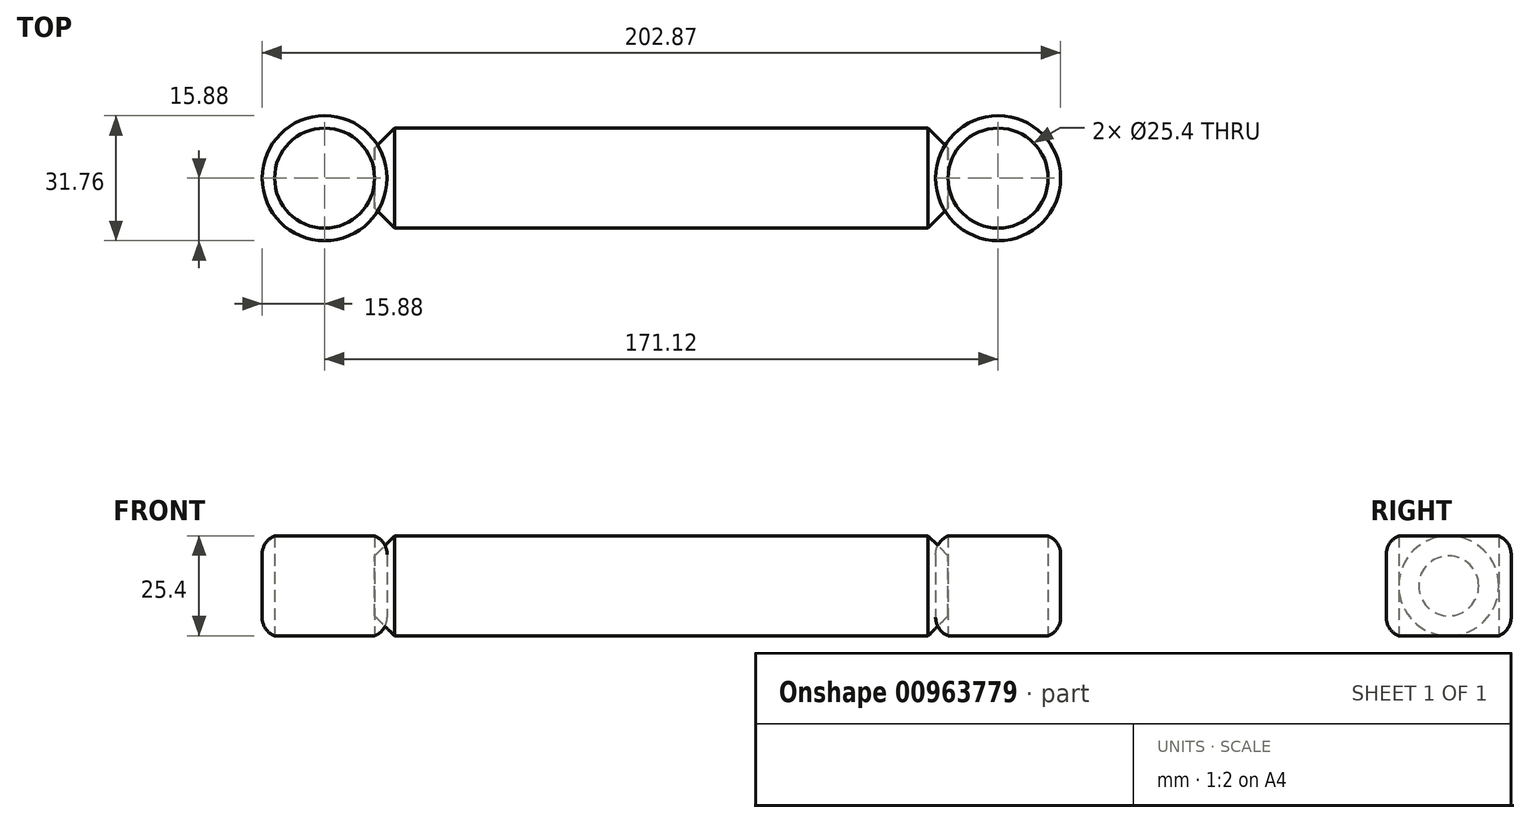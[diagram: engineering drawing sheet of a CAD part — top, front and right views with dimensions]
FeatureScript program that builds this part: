
annotation { "Feature Type Name" : "Feature", "Feature Type Description" : "" }
export const myFeature = defineFeature(function(context is Context, id is Id, definition is map)
    precondition{}
    {
        {
            var Q0;
            Q0=qCreatedBy(makeId("Top.planeOp"),FACE);
            var sketch = newSketch(context, id + "F0", { "sketchPlane" : qUnion([Q0])});
            skCircle(sketch, "E0", {"center": v(0, 0) * mm, "radius": 12.7 * mm});
            skCircle(sketch, "E1", {"center": v(171.12, 0) * mm, "radius": 12.7 * mm});
            skLineSegment(sketch, "E2", {"start": v(15.88, 0) * mm, "end": v(155.24, 0) * mm});
            skCircle(sketch, "E3", {"center": v(0, 0) * mm, "radius": 15.88 * mm});
            skCircle(sketch, "E4", {"center": v(171.12, 0) * mm, "radius": 15.88 * mm});
            skLineSegment(sketch, "E5", {"start": v(155.24, 0) * mm, "end": v(158.42, 0) * mm});
            skLineSegment(sketch, "E6", {"start": v(15.88, 0) * mm, "end": v(12.7, 0) * mm});
            skSolve(sketch);
        }
        {
            var Q0;
            Q0 = qSketchRegion(id + "F0", true);
            extrude(context, id + "F1", {"entities" : qUnion([Q0]), "endBound" : BoundingType.SYMMETRIC, "depth" : 25.4 * mm, "offsetDistance" : 25.4 * mm});
        }
        {
            var Q0;
            Q0=qCreatedBy(makeId("Right.planeOp"),FACE);
            cPlane(context, id + "F2", {"entities" : qUnion([Q0]), "cplaneType" : CPlaneType.OFFSET, "offset" : 12.7 * mm, "width" : 152.4 * mm, "height" : 152.4 * mm});
        }
        {
            var Q0;
            Q0=qCreatedBy(id+"F2.planeOp",FACE);
            var sketch = newSketch(context, id + "F3", { "sketchPlane" : qUnion([Q0])});
            skCircle(sketch, "E7", {"center": v(0, 0) * mm, "radius": 12.7 * mm});
            skSolve(sketch);
        }
        {
            var Q0;
            Q0 = qSketchRegion(id + "F3", true);
            var Q1;
            Q1=sQuery(id+"F0.wireOp",EDGE,"E6");
            var Q2;
            Q2=sQuery(id+"F0.wireOp",EDGE,"E2");
            var Q3;
            Q3=sQuery(id+"F0.wireOp",EDGE,"E5");
            sweep(context, id + "F4", {"profiles" : qUnion([Q0]), "path" : qUnion([Q1, Q2, Q3])});
        }
        {
            var Q0;
            Q0=makeQuery(id+"F1.opExtrude","CAP_EDGE",EDGE,{"disambiguationData":[OSD([sQuery(id+"F0.wireOp",EDGE,"E3")])],"isStart":false});
            var Q1;
            Q1=makeQuery(id+"F1.opExtrude","CAP_EDGE",EDGE,{"disambiguationData":[OSD([sQuery(id+"F0.wireOp",EDGE,"E3")])],"isStart":true});
            var Q2;
            Q2=makeQuery(id+"F1.opExtrude","CAP_EDGE",EDGE,{"disambiguationData":[OSD([sQuery(id+"F0.wireOp",EDGE,"E4")])],"isStart":false});
            var Q3;
            Q3=makeQuery(id+"F1.opExtrude","CAP_EDGE",EDGE,{"disambiguationData":[OSD([sQuery(id+"F0.wireOp",EDGE,"E4")])],"isStart":true});
            fillet(context, id + "F5", {"entities" : qUnion([Q0, Q1, Q2, Q3]), "radius" : 5.08 * mm, "tangentPropagation" : true, "allowEdgeOverflow" : false});
        }
        {
            var Q0;
            Q0=makeQuery(id+"F4.opSweep","CAP_EDGE",EDGE,{"disambiguationData":[OSD([sQuery(id+"F0.wireOp",VERTEX,"E5.end"),sQuery(id+"F3.wireOp",EDGE,"E7")])],"isStart":false});
            var Q1;
            Q1=makeQuery(id+"F4.opSweep","CAP_EDGE",EDGE,{"disambiguationData":[OSD([sQuery(id+"F0.wireOp",VERTEX,"E6.end"),sQuery(id+"F3.wireOp",EDGE,"E7")])],"isStart":true});
            chamfer(context, id + "F6", {"entities" : qUnion([Q0, Q1]), "width" : 5.08 * mm, "tangentPropagation" : true});
        }
    });
